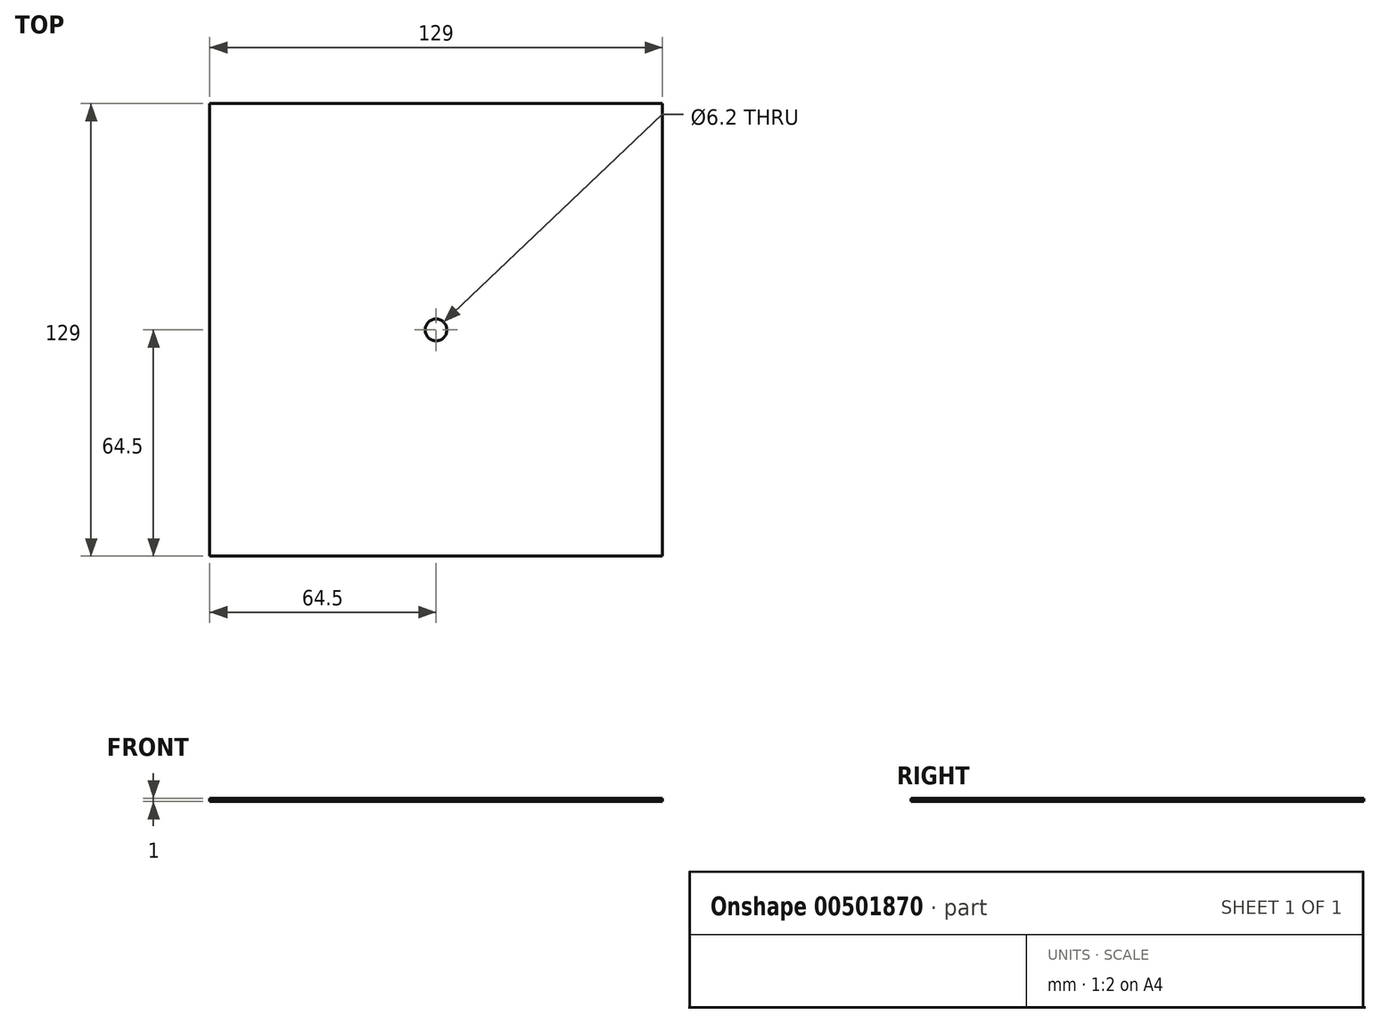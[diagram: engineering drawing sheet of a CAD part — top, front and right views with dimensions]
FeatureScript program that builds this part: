
annotation { "Feature Type Name" : "Feature", "Feature Type Description" : "" }
export const myFeature = defineFeature(function(context is Context, id is Id, definition is map)
    precondition{}
    {
        {
            var Q0;
            Q0=qCreatedBy(makeId("Top.planeOp"),FACE);
            var sketch = newSketch(context, id + "F0", { "sketchPlane" : qUnion([Q0])});
            skLineSegment(sketch, "E0.bottom", {"start": v(64.5, -64.5) * mm, "end": v(-64.5, -64.5) * mm});
            skLineSegment(sketch, "E0.top", {"start": v(64.5, 64.5) * mm, "end": v(-64.5, 64.5) * mm});
            skLineSegment(sketch, "E0.left", {"start": v(64.5, -64.5) * mm, "end": v(64.5, 64.5) * mm});
            skLineSegment(sketch, "E0.right", {"start": v(-64.5, -64.5) * mm, "end": v(-64.5, 64.5) * mm});
            skPoint(sketch, "E0.middle", {"position": v(0, 0) * mm});
            skCircle(sketch, "E1", {"center": v(0, 0) * mm, "radius": 3.1 * mm});
            skSolve(sketch);
        }
        {
            var Q0;
            Q0 = qSketchRegion(id + "F0", true);
            extrude(context, id + "F1", {"entities" : qUnion([Q0]), "depth" : 1 * mm});
        }
    });
